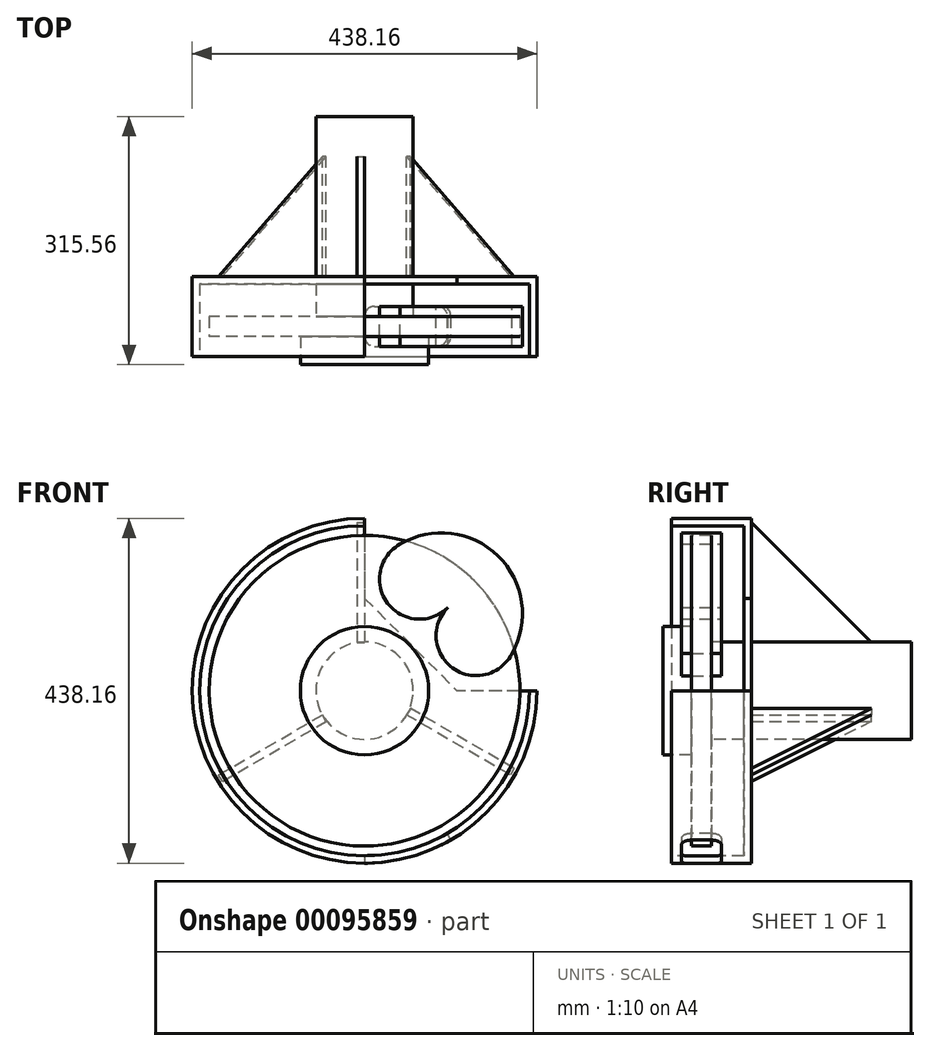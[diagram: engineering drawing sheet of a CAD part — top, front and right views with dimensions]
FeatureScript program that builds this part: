
annotation { "Feature Type Name" : "Feature", "Feature Type Description" : "" }
export const myFeature = defineFeature(function(context is Context, id is Id, definition is map)
    precondition{}
    {
        {
            var Q0;
            Q0=qCreatedBy(makeId("Top.planeOp"),FACE);
            var sketch = newSketch(context, id + "F0", { "sketchPlane" : qUnion([Q0])});
            skLineSegment(sketch, "E0", {"start": v(197.36, 0) * mm, "end": v(-197.36, 0) * mm, "construction": true});
            skPoint(sketch, "E1", {"position": v(0, 0) * mm});
            skLineSegment(sketch, "E2", {"start": v(-197.36, 12.7) * mm, "end": v(-197.36, -12.7) * mm});
            skLineSegment(sketch, "E3", {"start": v(-197.36, 12.7) * mm, "end": v(-61.87, 12.7) * mm});
            skLineSegment(sketch, "E4", {"start": v(-61.87, 12.7) * mm, "end": v(-61.87, 53.97) * mm});
            skLineSegment(sketch, "E5", {"start": v(-197.36, -12.7) * mm, "end": v(-81.5, -12.7) * mm});
            skLineSegment(sketch, "E6", {"start": v(-81.5, -12.7) * mm, "end": v(-81.5, -48.86) * mm});
            skLineSegment(sketch, "E7", {"start": v(-81.5, -48.86) * mm, "end": v(0, -48.86) * mm});
            skLineSegment(sketch, "E8", {"start": v(0, -48.86) * mm, "end": v(0, 266.7) * mm});
            skLineSegment(sketch, "E9", {"start": v(0, 266.7) * mm, "end": v(-61.87, 266.7) * mm});
            skLineSegment(sketch, "E10", {"start": v(-61.87, 63.5) * mm, "end": v(-209.55, 63.5) * mm});
            skLineSegment(sketch, "E11", {"start": v(0, 58.56) * mm, "end": v(-209.55, 58.56) * mm, "construction": true});
            skLineSegment(sketch, "E12", {"start": v(-209.55, 63.5) * mm, "end": v(-209.55, 58.56) * mm, "construction": true});
            skLineSegment(sketch, "E13", {"start": v(-209.55, 63.5) * mm, "end": v(-219.07, 63.5) * mm});
            skLineSegment(sketch, "E14", {"start": v(-219.07, 63.5) * mm, "end": v(-219.07, -38.1) * mm});
            skLineSegment(sketch, "E15", {"start": v(-135.71, 63.5) * mm, "end": v(-135.71, 53.97) * mm, "construction": true});
            skLineSegment(sketch, "E16", {"start": v(-219.07, -38.1) * mm, "end": v(-209.55, -38.1) * mm});
            skLineSegment(sketch, "E17", {"start": v(-209.55, -38.1) * mm, "end": v(-209.55, 53.97) * mm});
            skLineSegment(sketch, "E18", {"start": v(-209.55, 53.97) * mm, "end": v(-61.87, 53.97) * mm});
            skLineSegment(sketch, "E19.trimOffspring", {"start": v(-61.87, 63.5) * mm, "end": v(-61.87, 266.7) * mm});
            skSolve(sketch);
        }
        {
            var Q0;
            Q0=makeQuery(id+"F0.imprint","IMPRINT",FACE,{"disambiguationData":[TD([[makeQuery(id+"F0.imprint","IMPRINT",EDGE,{"derivedFrom":sQuery(id+"F0.wireOp",EDGE,"E2")}),1.0]])]});
            var Q1;
            Q1=sQuery(id+"F0.wireOp",EDGE,"E8");
            revolve(context, id + "F1", {"entities" : qUnion([Q0]), "axis" : qUnion([Q1]), "revolveType" : RevolveType.FULL});
        }
        {
            var Q0;
            Q0=makeQuery(id+"F1.opRevolve","SWEPT_FACE",FACE,{"disambiguationData":[OSD([sQuery(id+"F0.wireOp",EDGE,"E10"),sQuery(id+"F0.wireOp",EDGE,"E13")])]});
            var sketch = newSketch(context, id + "F2", { "sketchPlane" : qUnion([Q0])});
            skLineSegment(sketch, "E20", {"start": v(-219.07, 0) * mm, "end": v(-117.47, 0) * mm});
            skLineSegment(sketch, "E21", {"start": v(0, 219.07) * mm, "end": v(0, 117.47) * mm});
            skLineSegment(sketch, "E22", {"start": v(0, 117.47) * mm, "end": v(-117.47, 0) * mm});
            skLineSegment(sketch, "E23", {"start": v(0, 219.07) * mm, "end": v(-219.07, 219.07) * mm});
            skLineSegment(sketch, "E24", {"start": v(-219.07, 219.07) * mm, "end": v(-219.07, 0) * mm});
            skSolve(sketch);
        }
        {
            var Q0;
            Q0 = qSketchRegion(id + "F2", true);
            extrude(context, id + "F3", {"entities" : qUnion([Q0]), "operationType" : NewBodyOperationType.REMOVE, "oppositeDirection" : true, "depth" : 25.4 * mm});
        }
        {
            var Q0;
            Q0=makeQuery(id+"F3.boolean.opBoolean","COPY",FACE,{"derivedFrom":makeQuery(id+"F3.opExtrude","CAP_FACE",FACE,{"disambiguationData":[OSD([sQuery(id+"F2.wireOp",EDGE,"E20"),sQuery(id+"F2.wireOp",EDGE,"E21"),sQuery(id+"F2.wireOp",EDGE,"E22"),sQuery(id+"F2.wireOp",EDGE,"E23"),sQuery(id+"F2.wireOp",EDGE,"E24")])],"isStart":false})});
            var sketch = newSketch(context, id + "F4", { "sketchPlane" : qUnion([Q0])});
            skArc(sketch, "E25.0.0", {"start": v(0, 219.07) * mm, "mid": v(-154.9, 154.9) * mm, "end": v(-219.07, 0) * mm});
            skLineSegment(sketch, "E25.0.1", {"start": v(-219.07, 0) * mm, "end": v(-209.55, 0) * mm});
            skArc(sketch, "E25.0.2", {"start": v(-209.55, 0) * mm, "mid": v(-148.17, 148.17) * mm, "end": v(0, 209.55) * mm});
            skLineSegment(sketch, "E25.0.3", {"start": v(0, 209.55) * mm, "end": v(0, 219.07) * mm});
            skSolve(sketch);
        }
        {
            var Q0;
            Q0 = qSketchRegion(id + "F4", true);
            extrude(context, id + "F5", {"entities" : qUnion([Q0]), "operationType" : NewBodyOperationType.REMOVE, "endBound" : BoundingType.THROUGH_ALL, "oppositeDirection" : true, "depth" : 25.4 * mm});
        }
        {
            var Q0;
            Q0=qCreatedBy(makeId("Right.planeOp"),FACE);
            var sketch = newSketch(context, id + "F6", { "sketchPlane" : qUnion([Q0])});
            skLineSegment(sketch, "E26", {"start": v(0, 0) * mm, "end": v(63.5, 0) * mm, "construction": true});
            skLineSegment(sketch, "E27", {"start": v(63.5, 0) * mm, "end": v(63.5, 61.6) * mm, "construction": true});
            skLineSegment(sketch, "E28", {"start": v(63.5, 61.6) * mm, "end": v(215.9, 61.6) * mm});
            skLineSegment(sketch, "E29", {"start": v(215.9, 61.6) * mm, "end": v(63.5, 214) * mm});
            skLineSegment(sketch, "E30", {"start": v(63.5, 214) * mm, "end": v(63.5, 61.6) * mm});
            skSolve(sketch);
        }
        {
            var Q0;
            Q0 = qSketchRegion(id + "F6", true);
            extrude(context, id + "F7", {"entities" : qUnion([Q0]), "oppositeDirection" : true, "depth" : 9.52 * mm});
        }
        {
            var Q0;
            Q0=makeQuery(id+"F7.opExtrude","SWEPT_BODY",BODY,{"disambiguationData":[OSD([sQuery(id+"F6.wireOp",EDGE,"E28"),sQuery(id+"F6.wireOp",EDGE,"E29"),sQuery(id+"F6.wireOp",EDGE,"E30")])]});
            var Q1;
            Q1=makeQuery(id+"F1.opRevolve","SWEPT_EDGE",EDGE,{"disambiguationData":[OSD([sQuery(id+"F0.wireOp",EDGE,"E9"),sQuery(id+"F0.wireOp",EDGE,"E19.trimOffspring")])]});
            circularPattern(context, id + "F8", {"entities" : qUnion([Q0]), "axis" : qUnion([Q1]), "angle" : 360 * degree, "instanceCount" : 3, "equalSpace" : true, "computeTransformsWithoutBuiltin" : true});
        }
        {
            var Q0;
            Q0=makeQuery(id+"F1.opRevolve","SWEPT_FACE",FACE,{"disambiguationData":[OSD([sQuery(id+"F0.wireOp",EDGE,"E5")])]});
            var sketch = newSketch(context, id + "F9", { "sketchPlane" : qUnion([Q0])});
            skArc(sketch, "E31", {"start": v(45.22, 186.13) * mm, "mid": v(31.98, 107.88) * mm, "end": v(111.23, 112.22) * mm});
            skArc(sketch, "E32", {"start": v(112.22, 111.23) * mm, "mid": v(108.64, 31.31) * mm, "end": v(187.09, 47.02) * mm});
            skCircle(sketch, "E33", {"center": v(0, 0) * mm, "radius": 158 * mm, "construction": true});
            skLineSegment(sketch, "E34", {"start": v(141.71, 69.87) * mm, "end": v(69.87, 141.71) * mm});
            skLineSegment(sketch, "E35", {"start": v(0, 0) * mm, "end": v(105.8, 105.8) * mm, "construction": true});
            skLineSegment(sketch, "E36", {"start": v(0, 0) * mm, "end": v(98.73, 0) * mm, "construction": true});
            skArc(sketch, "E37", {"start": v(181.62, 38.44) * mm, "mid": v(171.17, 169.75) * mm, "end": v(40.1, 182.87) * mm});
            skSolve(sketch);
        }
        {
            var Q0;
            Q0 = qSketchRegion(id + "F9", true);
            extrude(context, id + "F10", {"entities" : qUnion([Q0]), "depth" : 12.7 * mm, "hasSecondDirection" : true, "secondDirectionOppositeDirection" : true, "secondDirectionDepth" : 38.1 * mm});
        }
        {
            var Q0;
            Q0=qCreatedBy(makeId("Front.planeOp"),FACE);
            var sketch = newSketch(context, id + "F11", { "sketchPlane" : qUnion([Q0])});
            skArc(sketch, "E38", {"start": v(0, -203.2) * mm, "mid": v(52.6, -196.28) * mm, "end": v(101.6, -175.98) * mm});
            skArc(sketch, "E39", {"start": v(0, -230.31) * mm, "mid": v(59.6, -222.47) * mm, "end": v(115.16, -199.46) * mm});
            skLineSegment(sketch, "E40", {"start": v(0, 0) * mm, "end": v(0, -203.2) * mm, "construction": true});
            skLineSegment(sketch, "E41", {"start": v(0, 0) * mm, "end": v(101.6, -175.98) * mm, "construction": true});
            skLineSegment(sketch, "E42", {"start": v(0, -203.2) * mm, "end": v(0, -230.31) * mm});
            skLineSegment(sketch, "E43", {"start": v(101.6, -175.98) * mm, "end": v(115.16, -199.46) * mm});
            skSolve(sketch);
        }
        {
            var Q0;
            Q0 = qSketchRegion(id + "F11", true);
            extrude(context, id + "F12", {"entities" : qUnion([Q0]), "operationType" : NewBodyOperationType.REMOVE, "depth" : 25.4 * mm, "hasSecondDirection" : true, "secondDirectionOppositeDirection" : true, "secondDirectionDepth" : 25.4 * mm});
        }
        {
            var Q0;
            Q0=makeQuery(id+"F12.boolean.opBoolean","COPY",EDGE,{"derivedFrom":makeQuery(id+"F12.opExtrude","CAP_EDGE",EDGE,{"disambiguationData":[OSD([sQuery(id+"F11.wireOp",EDGE,"E42")])],"isStart":true})});
            var Q1;
            Q1=makeQuery(id+"F12.boolean.opBoolean","COPY",EDGE,{"derivedFrom":makeQuery(id+"F12.opExtrude","CAP_EDGE",EDGE,{"disambiguationData":[OSD([sQuery(id+"F11.wireOp",EDGE,"E43")])],"isStart":true})});
            var Q2;
            Q2=makeQuery(id+"F12.boolean.opBoolean","COPY",EDGE,{"derivedFrom":makeQuery(id+"F12.opExtrude","CAP_EDGE",EDGE,{"disambiguationData":[OSD([sQuery(id+"F11.wireOp",EDGE,"E43")])],"isStart":false})});
            var Q3;
            Q3=makeQuery(id+"F12.boolean.opBoolean","COPY",EDGE,{"derivedFrom":makeQuery(id+"F12.opExtrude","CAP_EDGE",EDGE,{"disambiguationData":[OSD([sQuery(id+"F11.wireOp",EDGE,"E42")])],"isStart":false})});
            fillet(context, id + "F13", {"entities" : qUnion([Q0, Q1, Q2, Q3]), "radius" : 12.7 * mm, "tangentPropagation" : true, "allowEdgeOverflow" : false});
        }
    });
